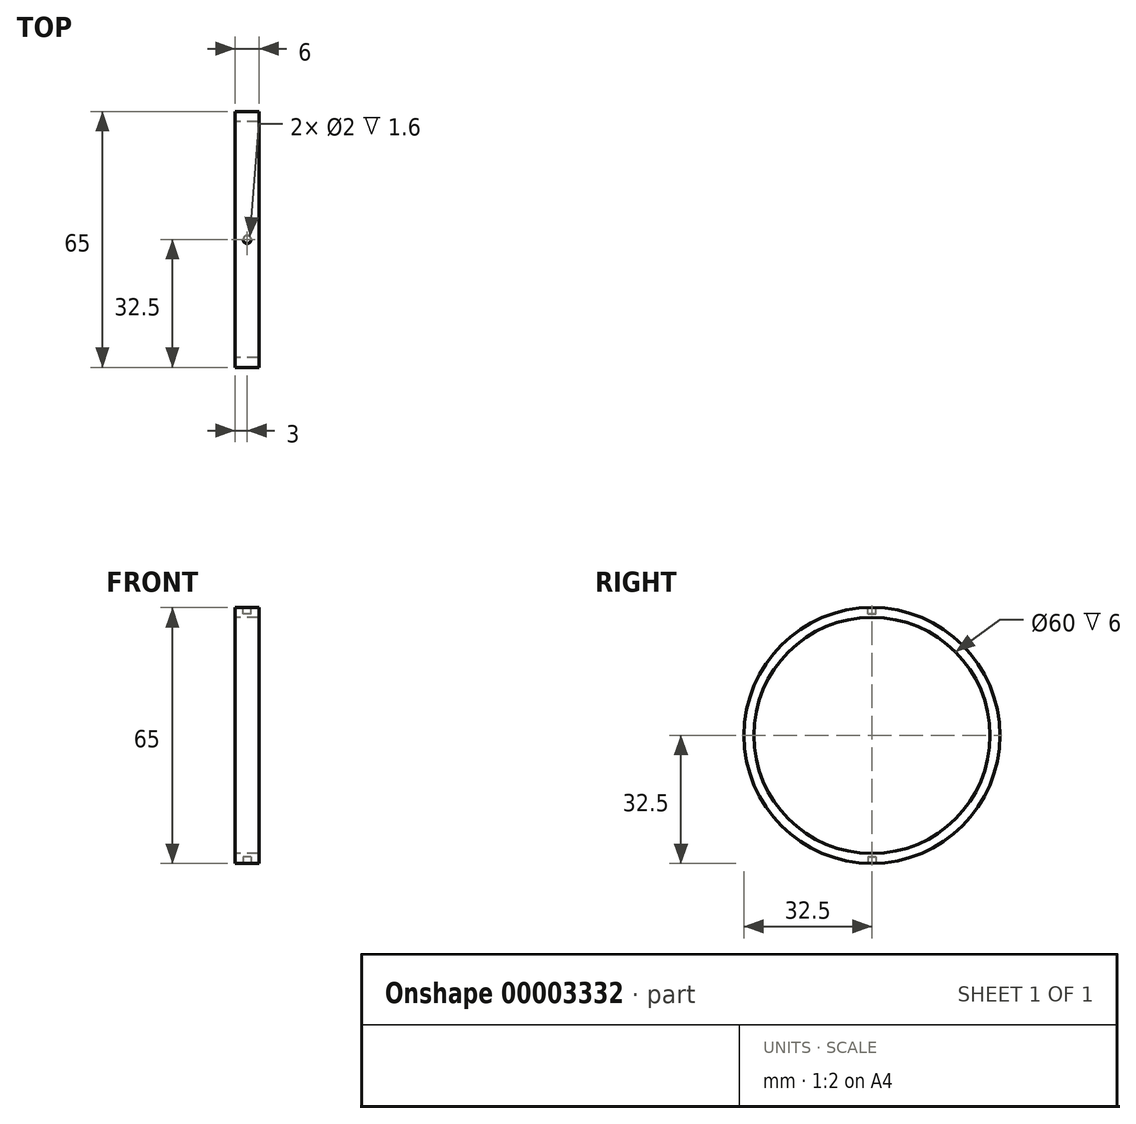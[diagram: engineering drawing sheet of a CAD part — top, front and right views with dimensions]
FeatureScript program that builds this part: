
annotation { "Feature Type Name" : "Feature", "Feature Type Description" : "" }
export const myFeature = defineFeature(function(context is Context, id is Id, definition is map)
    precondition{}
    {
        {
            var Q0;
            Q0=qCreatedBy(makeId("Front.planeOp"),FACE);
            var sketch = newSketch(context, id + "F0", { "sketchPlane" : qUnion([Q0])});
            skLineSegment(sketch, "E0", {"start": v(0, 0) * mm, "end": v(6, 0) * mm});
            skLineSegment(sketch, "E1", {"start": v(0, 30) * mm, "end": v(6, 30) * mm});
            skLineSegment(sketch, "E2", {"start": v(6, 30) * mm, "end": v(6, 32.5) * mm});
            skLineSegment(sketch, "E3", {"start": v(6, 32.5) * mm, "end": v(0, 32.5) * mm});
            skLineSegment(sketch, "E4", {"start": v(0, 32.5) * mm, "end": v(0, 30) * mm});
            skLineSegment(sketch, "E5.0.MirrorCS", {"start": v(0, -30) * mm, "end": v(6, -30) * mm});
            skLineSegment(sketch, "E6.0.MirrorCS", {"start": v(6, -30) * mm, "end": v(6, -32.5) * mm});
            skLineSegment(sketch, "E7.0.MirrorCS", {"start": v(0, -32.5) * mm, "end": v(0, -30) * mm});
            skLineSegment(sketch, "E8.0.MirrorCS", {"start": v(6, -32.5) * mm, "end": v(0, -32.5) * mm});
            skSolve(sketch);
        }
        {
            var Q0;
            Q0=makeQuery(id+"F0.imprint","IMPRINT",FACE,{"disambiguationData":[TD([[makeQuery(id+"F0.imprint","IMPRINT",EDGE,{"derivedFrom":sQuery(id+"F0.wireOp",EDGE,"E1")}),1.0]])]});
            var Q1;
            Q1=sQuery(id+"F0.wireOp",EDGE,"E0");
            revolve(context, id + "F1", {"entities" : qUnion([Q0]), "axis" : qUnion([Q1]), "revolveType" : RevolveType.FULL});
        }
        {
            var Q0;
            Q0=qCreatedBy(makeId("Top.planeOp"),FACE);
            cPlane(context, id + "F2", {"entities" : qUnion([Q0]), "cplaneType" : CPlaneType.OFFSET, "offset" : (65 / 2) * mm, "width" : 150 * mm, "height" : 150 * mm});
        }
        {
            var Q0;
            Q0=qCreatedBy(id+"F2.planeOp",FACE);
            var sketch = newSketch(context, id + "F3", { "sketchPlane" : qUnion([Q0])});
            skLineSegment(sketch, "E9.0", {"start": v(0, -32.5) * mm, "end": v(0, 32.5) * mm, "construction": true});
            skLineSegment(sketch, "E10.0", {"start": v(6, -32.5) * mm, "end": v(6, 32.5) * mm, "construction": true});
            skLineSegment(sketch, "E11", {"start": v(0, 0) * mm, "end": v(6, 0) * mm, "construction": true});
            skCircle(sketch, "E12", {"center": v(3, 0) * mm, "radius": 1 * mm});
            skSolve(sketch);
        }
        {
            var Q0;
            Q0=makeQuery(id+"F3.imprint","IMPRINT",FACE,{"disambiguationData":[TD([[makeQuery(id+"F3.imprint","IMPRINT",EDGE,{"derivedFrom":sQuery(id+"F3.wireOp",EDGE,"E12")}),1.0]])]});
            extrude(context, id + "F4", {"entities" : qUnion([Q0]), "operationType" : NewBodyOperationType.REMOVE, "oppositeDirection" : true, "depth" : 1.6 * mm});
        }
        {
            var Q0;
            Q0=makeQuery(id+"F4.boolean.opBoolean","COPY",FACE,{"derivedFrom":makeQuery(id+"F4.opExtrude","SWEPT_FACE",FACE,{"disambiguationData":[OSD([sQuery(id+"F3.wireOp",EDGE,"E12")])]})});
            var Q1;
            Q1=makeQuery(id+"F4.boolean.opBoolean","COPY",FACE,{"derivedFrom":makeQuery(id+"F4.opExtrude","CAP_FACE",FACE,{"disambiguationData":[OSD([sQuery(id+"F3.wireOp",EDGE,"E12")])],"isStart":false})});
            var Q2;
            Q2=qCreatedBy(makeId("Top.planeOp"),FACE);
            mirror(context, id + "F5", {"faces" : qUnion([Q0, Q1]), "mirrorPlane" : qUnion([Q2]), "patternType" : MirrorType.FACE});
        }
    });
